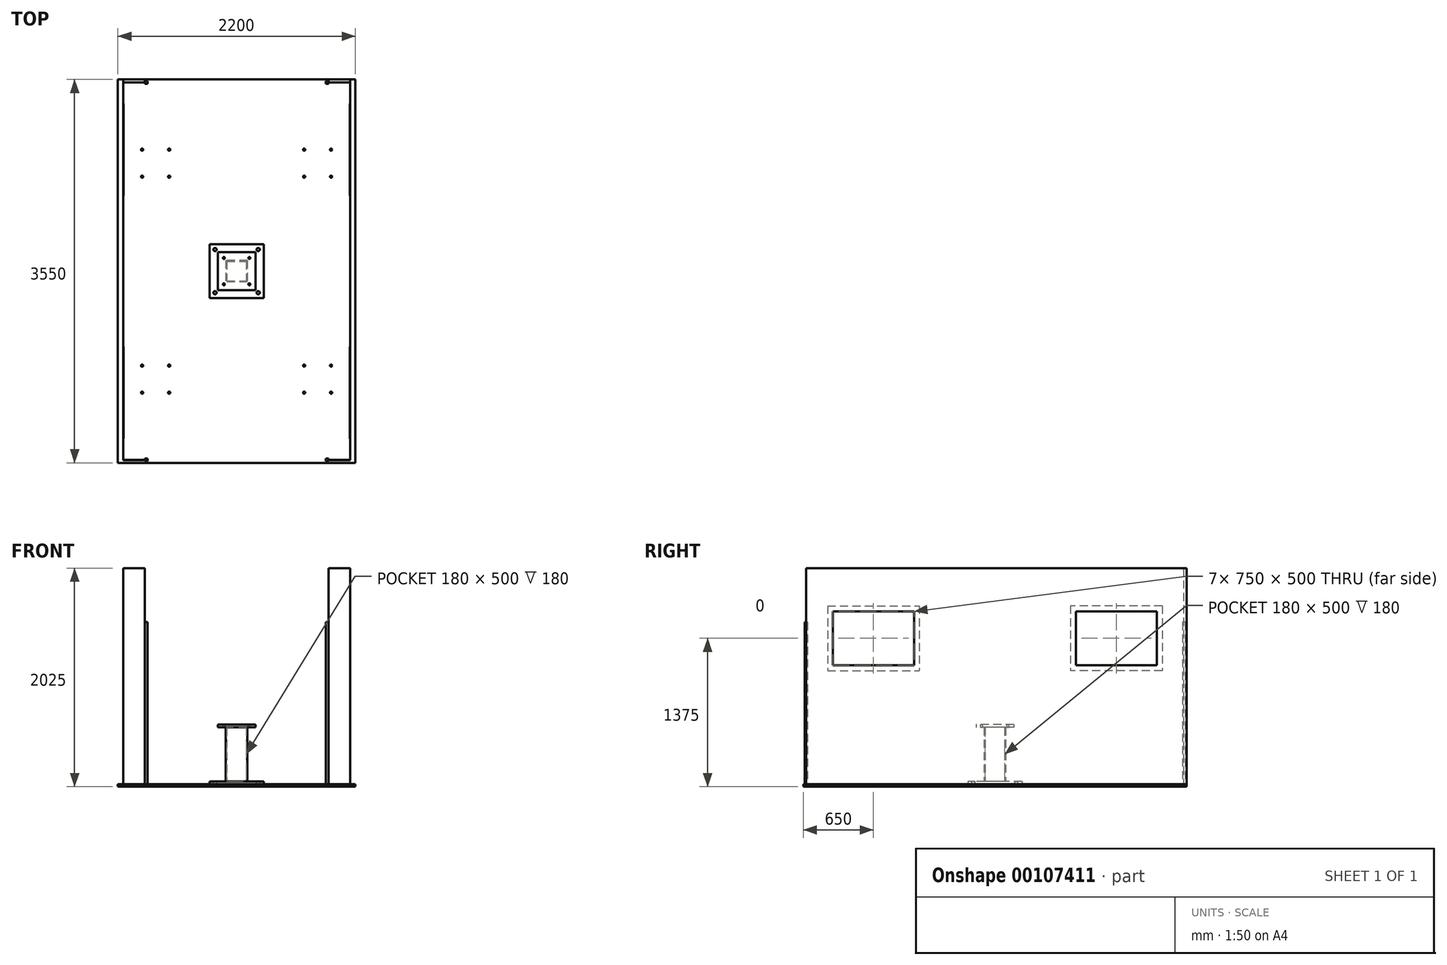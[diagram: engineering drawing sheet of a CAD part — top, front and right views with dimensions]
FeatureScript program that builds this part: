
annotation { "Feature Type Name" : "Feature", "Feature Type Description" : "" }
export const myFeature = defineFeature(function(context is Context, id is Id, definition is map)
    precondition{}
    {
        {
            var Q0;
            Q0=qCreatedBy(makeId("Top.planeOp"),FACE);
            var sketch = newSketch(context, id + "F0", { "sketchPlane" : qUnion([Q0])});
            skLineSegment(sketch, "E0.bottom", {"start": v(-1100, 1750) * mm, "end": v(1100, 1750) * mm});
            skLineSegment(sketch, "E0.top", {"start": v(-1100, -1750) * mm, "end": v(1100, -1750) * mm});
            skLineSegment(sketch, "E0.left", {"start": v(-1100, 1750) * mm, "end": v(-1100, -1750) * mm});
            skLineSegment(sketch, "E0.right", {"start": v(1100, 1750) * mm, "end": v(1100, -1750) * mm});
            skPoint(sketch, "E0.middle", {"position": v(0, 0) * mm});
            skSolve(sketch);
        }
        {
            var Q0;
            Q0 = qSketchRegion(id + "F0", true);
            extrude(context, id + "F1", {"entities" : qUnion([Q0]), "depth" : 25 * mm});
        }
        {
            var Q0;
            Q0=makeQuery(id+"F1.opExtrude","CAP_FACE",FACE,{"disambiguationData":[OSD([sQuery(id+"F0.wireOp",EDGE,"E0.bottom"),sQuery(id+"F0.wireOp",EDGE,"E0.top"),sQuery(id+"F0.wireOp",EDGE,"E0.left"),sQuery(id+"F0.wireOp",EDGE,"E0.right")])],"isStart":false});
            var sketch = newSketch(context, id + "F2", { "sketchPlane" : qUnion([Q0])});
            skLineSegment(sketch, "E1.bottom", {"start": v(-250, 250) * mm, "end": v(250, 250) * mm});
            skLineSegment(sketch, "E1.top", {"start": v(-250, -250) * mm, "end": v(250, -250) * mm});
            skLineSegment(sketch, "E1.left", {"start": v(-250, 250) * mm, "end": v(-250, -250) * mm});
            skLineSegment(sketch, "E1.right", {"start": v(250, 250) * mm, "end": v(250, -250) * mm});
            skPoint(sketch, "E1.middle", {"position": v(0, 0) * mm});
            skSolve(sketch);
        }
        {
            var Q0;
            Q0 = qSketchRegion(id + "F2", true);
            var Q1;
            Q1=makeQuery(id+"F2.imprint","IMPRINT",FACE,{"disambiguationData":[TD([[makeQuery(id+"F2.imprint","IMPRINT",EDGE,{"derivedFrom":sQuery(id+"F2.wireOp",EDGE,"E1.bottom")}),-1.0]])]});
            extrude(context, id + "F3", {"entities" : qUnion([Q0, Q1]), "depth" : 25 * mm});
        }
        {
            var Q0;
            Q0=makeQuery(id+"F3.opExtrude","CAP_FACE",FACE,{"disambiguationData":[OSD([sQuery(id+"F2.wireOp",EDGE,"E1.bottom"),sQuery(id+"F2.wireOp",EDGE,"E1.top"),sQuery(id+"F2.wireOp",EDGE,"E1.left"),sQuery(id+"F2.wireOp",EDGE,"E1.right")])],"isStart":false});
            var sketch = newSketch(context, id + "F4", { "sketchPlane" : qUnion([Q0])});
            skLineSegment(sketch, "E2.bottom", {"start": v(-200, 200) * mm, "end": v(200, 200) * mm, "construction": true});
            skLineSegment(sketch, "E2.top", {"start": v(-200, -200) * mm, "end": v(200, -200) * mm, "construction": true});
            skLineSegment(sketch, "E2.left", {"start": v(-200, 200) * mm, "end": v(-200, -200) * mm, "construction": true});
            skLineSegment(sketch, "E2.right", {"start": v(200, 200) * mm, "end": v(200, -200) * mm, "construction": true});
            skPoint(sketch, "E2.middle", {"position": v(0, 0) * mm});
            skCircle(sketch, "E3", {"center": v(-200, 200) * mm, "radius": 15 * mm});
            skCircle(sketch, "E4", {"center": v(200, 200) * mm, "radius": 15 * mm});
            skCircle(sketch, "E5", {"center": v(200, -200) * mm, "radius": 15 * mm});
            skCircle(sketch, "E6", {"center": v(-200, -200) * mm, "radius": 15 * mm});
            skSolve(sketch);
        }
        {
            var Q0;
            Q0 = qSketchRegion(id + "F4", true);
            extrude(context, id + "F5", {"entities" : qUnion([Q0]), "operationType" : NewBodyOperationType.REMOVE, "endBound" : BoundingType.THROUGH_ALL, "oppositeDirection" : true, "depth" : 25 * mm});
        }
        {
            var Q0;
            Q0=makeQuery(id+"F3.opExtrude","CAP_FACE",FACE,{"disambiguationData":[OSD([sQuery(id+"F2.wireOp",EDGE,"E1.bottom"),sQuery(id+"F2.wireOp",EDGE,"E1.top"),sQuery(id+"F2.wireOp",EDGE,"E1.left"),sQuery(id+"F2.wireOp",EDGE,"E1.right")])],"isStart":false});
            var sketch = newSketch(context, id + "F6", { "sketchPlane" : qUnion([Q0])});
            skLineSegment(sketch, "E7.bottom", {"start": v(100, 100) * mm, "end": v(-100, 100) * mm});
            skLineSegment(sketch, "E7.top", {"start": v(100, -100) * mm, "end": v(-100, -100) * mm});
            skLineSegment(sketch, "E7.left", {"start": v(100, 100) * mm, "end": v(100, -100) * mm});
            skLineSegment(sketch, "E7.right", {"start": v(-100, 100) * mm, "end": v(-100, -100) * mm});
            skPoint(sketch, "E7.middle", {"position": v(0, 0) * mm});
            skLineSegment(sketch, "E8.bottom", {"start": v(-90, 90) * mm, "end": v(90, 90) * mm});
            skLineSegment(sketch, "E8.top", {"start": v(-90, -90) * mm, "end": v(90, -90) * mm});
            skLineSegment(sketch, "E8.left", {"start": v(-90, 90) * mm, "end": v(-90, -90) * mm});
            skLineSegment(sketch, "E8.right", {"start": v(90, 90) * mm, "end": v(90, -90) * mm});
            skSolve(sketch);
        }
        {
            var Q0;
            Q0=makeQuery(id+"F6.imprint","IMPRINT",FACE,{"disambiguationData":[TD([[makeQuery(id+"F6.imprint","IMPRINT",EDGE,{"derivedFrom":sQuery(id+"F6.wireOp",EDGE,"E7.bottom")}),1.0]])]});
            extrude(context, id + "F7", {"entities" : qUnion([Q0]), "operationType" : NewBodyOperationType.ADD, "depth" : 500 * mm});
        }
        {
            var Q0;
            Q0=makeQuery(id+"F7.opExtrude","CAP_FACE",FACE,{"disambiguationData":[OSD([sQuery(id+"F6.wireOp",EDGE,"E7.bottom"),sQuery(id+"F6.wireOp",EDGE,"E7.top"),sQuery(id+"F6.wireOp",EDGE,"E7.left"),sQuery(id+"F6.wireOp",EDGE,"E7.right"),sQuery(id+"F6.wireOp",EDGE,"E8.bottom"),sQuery(id+"F6.wireOp",EDGE,"E8.top"),sQuery(id+"F6.wireOp",EDGE,"E8.left"),sQuery(id+"F6.wireOp",EDGE,"E8.right")])],"isStart":false});
            var sketch = newSketch(context, id + "F8", { "sketchPlane" : qUnion([Q0])});
            skLineSegment(sketch, "E9.bottom", {"start": v(175, 175) * mm, "end": v(-175, 175) * mm});
            skLineSegment(sketch, "E9.top", {"start": v(175, -175) * mm, "end": v(-175, -175) * mm});
            skLineSegment(sketch, "E9.left", {"start": v(175, 175) * mm, "end": v(175, -175) * mm});
            skLineSegment(sketch, "E9.right", {"start": v(-175, 175) * mm, "end": v(-175, -175) * mm});
            skPoint(sketch, "E9.middle", {"position": v(0, 0) * mm});
            skSolve(sketch);
        }
        {
            var Q0;
            Q0 = qSketchRegion(id + "F8", true);
            extrude(context, id + "F9", {"entities" : qUnion([Q0]), "operationType" : NewBodyOperationType.ADD, "depth" : 25 * mm});
        }
        {
            var Q0;
            Q0=makeQuery(id+"F1.opExtrude","CAP_FACE",FACE,{"disambiguationData":[OSD([sQuery(id+"F0.wireOp",EDGE,"E0.bottom"),sQuery(id+"F0.wireOp",EDGE,"E0.top"),sQuery(id+"F0.wireOp",EDGE,"E0.left"),sQuery(id+"F0.wireOp",EDGE,"E0.right")])],"isStart":false});
            var sketch = newSketch(context, id + "F10", { "sketchPlane" : qUnion([Q0])});
            skLineSegment(sketch, "E10.0", {"start": v(1100, 1750) * mm, "end": v(1100, -1750) * mm, "construction": true});
            skLineSegment(sketch, "E11.0", {"start": v(1050, 1750) * mm, "end": v(1050, -1748) * mm});
            skLineSegment(sketch, "E12", {"start": v(1050, 1750) * mm, "end": v(850, 1750) * mm});
            skLineSegment(sketch, "E13", {"start": v(1050, -1750) * mm, "end": v(850, -1750) * mm});
            skLineSegment(sketch, "E14", {"start": v(850, 1750) * mm, "end": v(850, 1748) * mm});
            skLineSegment(sketch, "E15", {"start": v(850, 1748) * mm, "end": v(1050, 1748) * mm});
            skLineSegment(sketch, "E16.0", {"start": v(1052, 1750) * mm, "end": v(1052, -1750) * mm});
            skLineSegment(sketch, "E17.0", {"start": v(1050, -1748) * mm, "end": v(850, -1748) * mm});
            skLineSegment(sketch, "E18", {"start": v(850, -1748) * mm, "end": v(850, -1750) * mm});
            skLineSegment(sketch, "E19", {"start": v(1052, -1750) * mm, "end": v(1050, -1750) * mm});
            skLineSegment(sketch, "E20", {"start": v(0, 1750) * mm, "end": v(0, -1750) * mm, "construction": true});
            skLineSegment(sketch, "E21.MirrorCS", {"start": v(-1052, -1750) * mm, "end": v(-1050, -1750) * mm});
            skLineSegment(sketch, "E22.MirrorCS", {"start": v(-850, 1750) * mm, "end": v(-850, 1748) * mm});
            skLineSegment(sketch, "E23.MirrorCS", {"start": v(-850, -1748) * mm, "end": v(-850, -1750) * mm});
            skLineSegment(sketch, "E24.MirrorCS", {"start": v(-1050, -1750) * mm, "end": v(-850, -1750) * mm});
            skLineSegment(sketch, "E25.MirrorCS", {"start": v(-1050, -1748) * mm, "end": v(-850, -1748) * mm});
            skLineSegment(sketch, "E26.MirrorCS", {"start": v(-1050, 1750) * mm, "end": v(-850, 1750) * mm});
            skLineSegment(sketch, "E27.MirrorCS", {"start": v(-1050, 1750) * mm, "end": v(-1050, -1748) * mm});
            skLineSegment(sketch, "E28.MirrorCS", {"start": v(-1100, 1750) * mm, "end": v(-1100, -1750) * mm, "construction": true});
            skLineSegment(sketch, "E29.MirrorCS", {"start": v(-850, 1748) * mm, "end": v(-1050, 1748) * mm});
            skLineSegment(sketch, "E30.MirrorCS", {"start": v(-1052, 1750) * mm, "end": v(-1052, -1750) * mm});
            skSolve(sketch);
        }
        {
            var Q0;
            Q0 = qSketchRegion(id + "F10", true);
            var Q1;
            Q1=makeQuery(id+"F10.imprint","IMPRINT",FACE,{"disambiguationData":[TD([[makeQuery(id+"F10.imprint","IMPRINT",EDGE,{"derivedFrom":sQuery(id+"F10.wireOp",EDGE,"E21.MirrorCS")}),1.0]])]});
            var Q2;
            Q2=makeQuery(id+"F10.imprint","IMPRINT",FACE,{"disambiguationData":[TD([[makeQuery(id+"F10.imprint","IMPRINT",EDGE,{"derivedFrom":sQuery(id+"F10.wireOp",EDGE,"E13")}),1.0]])]});
            extrude(context, id + "F11", {"entities" : qUnion([Q0, Q1, Q2]), "depth" : 2000 * mm});
        }
        {
            var Q0;
            Q0=makeQuery(id+"F11.opExtrude","SWEPT_FACE",FACE,{"disambiguationData":[OSD([sQuery(id+"F10.wireOp",EDGE,"E16.0")])]});
            var sketch = newSketch(context, id + "F12", { "sketchPlane" : qUnion([Q0])});
            skLineSegment(sketch, "E31.bottom", {"start": v(-1500, 1625) * mm, "end": v(-750, 1625) * mm});
            skLineSegment(sketch, "E31.top", {"start": v(-1500, 1125) * mm, "end": v(-750, 1125) * mm});
            skLineSegment(sketch, "E31.left", {"start": v(-1500, 1625) * mm, "end": v(-1500, 1125) * mm});
            skLineSegment(sketch, "E31.right", {"start": v(-750, 1625) * mm, "end": v(-750, 1125) * mm});
            skLineSegment(sketch, "E32", {"start": v(0, 0) * mm, "end": v(0, 2025) * mm, "construction": true});
            skLineSegment(sketch, "E33.MirrorCS", {"start": v(1500, 1625) * mm, "end": v(750, 1625) * mm});
            skLineSegment(sketch, "E34.MirrorCS", {"start": v(1500, 1125) * mm, "end": v(750, 1125) * mm});
            skLineSegment(sketch, "E35.MirrorCS", {"start": v(1500, 1625) * mm, "end": v(1500, 1125) * mm});
            skLineSegment(sketch, "E36.MirrorCS", {"start": v(750, 1625) * mm, "end": v(750, 1125) * mm});
            skSolve(sketch);
        }
        {
            var Q0;
            Q0=makeQuery(id+"F11.opExtrude","SWEPT_FACE",FACE,{"disambiguationData":[OSD([sQuery(id+"F10.wireOp",EDGE,"E30.MirrorCS")])]});
            var sketch = newSketch(context, id + "F13", { "sketchPlane" : qUnion([Q0])});
            skLineSegment(sketch, "E37.0", {"start": v(-1500, 1625) * mm, "end": v(-750, 1625) * mm});
            skLineSegment(sketch, "E37.1", {"start": v(-1500, 1125) * mm, "end": v(-750, 1125) * mm});
            skLineSegment(sketch, "E37.2", {"start": v(-1500, 1625) * mm, "end": v(-1500, 1125) * mm});
            skLineSegment(sketch, "E37.3", {"start": v(-750, 1625) * mm, "end": v(-750, 1125) * mm});
            skLineSegment(sketch, "E38.0", {"start": v(1500, 1625) * mm, "end": v(750, 1625) * mm});
            skLineSegment(sketch, "E38.1", {"start": v(1500, 1125) * mm, "end": v(750, 1125) * mm});
            skLineSegment(sketch, "E38.2", {"start": v(1500, 1625) * mm, "end": v(1500, 1125) * mm});
            skLineSegment(sketch, "E38.3", {"start": v(750, 1625) * mm, "end": v(750, 1125) * mm});
            skLineSegment(sketch, "E39.0", {"start": v(0, 0) * mm, "end": v(0, 2025) * mm, "construction": true});
            skSolve(sketch);
        }
        {
            var Q0;
            Q0=makeQuery(id+"F13.imprint","IMPRINT",FACE,{"disambiguationData":[TD([[makeQuery(id+"F13.imprint","IMPRINT",EDGE,{"derivedFrom":sQuery(id+"F13.wireOp",EDGE,"E38.0")}),1.0]])]});
            var Q1;
            Q1=makeQuery(id+"F13.imprint","IMPRINT",FACE,{"disambiguationData":[TD([[makeQuery(id+"F13.imprint","IMPRINT",EDGE,{"derivedFrom":sQuery(id+"F13.wireOp",EDGE,"E37.0")}),-1.0]])]});
            var Q2;
            Q2=makeQuery(id+"F11.opExtrude","SWEPT_FACE",FACE,{"disambiguationData":[OSD([sQuery(id+"F10.wireOp",EDGE,"E27.MirrorCS")])]});
            extrude(context, id + "F14", {"entities" : qUnion([Q0, Q1]), "operationType" : NewBodyOperationType.REMOVE, "endBound" : BoundingType.UP_TO_SURFACE, "oppositeDirection" : true, "endBoundEntityFace" : qUnion([Q2]), "depth" : 25 * mm});
        }
        {
            var Q0;
            Q0=makeQuery(id+"F12.imprint","IMPRINT",FACE,{"disambiguationData":[TD([[makeQuery(id+"F12.imprint","IMPRINT",EDGE,{"derivedFrom":sQuery(id+"F12.wireOp",EDGE,"E31.bottom")}),-1.0]])]});
            var Q1;
            Q1=makeQuery(id+"F12.imprint","IMPRINT",FACE,{"disambiguationData":[TD([[makeQuery(id+"F12.imprint","IMPRINT",EDGE,{"derivedFrom":sQuery(id+"F12.wireOp",EDGE,"E33.MirrorCS")}),1.0]])]});
            var Q2;
            Q2=makeQuery(id+"F11.opExtrude","SWEPT_FACE",FACE,{"disambiguationData":[OSD([sQuery(id+"F10.wireOp",EDGE,"E11.0")])]});
            extrude(context, id + "F15", {"entities" : qUnion([Q0, Q1]), "operationType" : NewBodyOperationType.REMOVE, "endBound" : BoundingType.UP_TO_SURFACE, "oppositeDirection" : true, "endBoundEntityFace" : qUnion([Q2]), "depth" : 25 * mm});
        }
        {
            var Q0;
            Q0=makeQuery(id+"F11.opExtrude","SWEPT_FACE",FACE,{"disambiguationData":[OSD([sQuery(id+"F10.wireOp",EDGE,"E27.MirrorCS")])]});
            var sketch = newSketch(context, id + "F16", { "sketchPlane" : qUnion([Q0])});
            skLineSegment(sketch, "E40.bottom", {"start": v(-1550, 1675) * mm, "end": v(-700, 1675) * mm});
            skLineSegment(sketch, "E40.top", {"start": v(-1550, 1075) * mm, "end": v(-700, 1075) * mm});
            skLineSegment(sketch, "E40.left", {"start": v(-1550, 1675) * mm, "end": v(-1550, 1075) * mm});
            skLineSegment(sketch, "E40.right", {"start": v(-700, 1675) * mm, "end": v(-700, 1075) * mm});
            skLineSegment(sketch, "E41.0", {"start": v(-1500, 1625) * mm, "end": v(-750, 1625) * mm, "construction": true});
            skLineSegment(sketch, "E42.0", {"start": v(-1500, 1125) * mm, "end": v(-750, 1125) * mm, "construction": true});
            skLineSegment(sketch, "E43.0", {"start": v(-1500, 1625) * mm, "end": v(-1500, 1125) * mm, "construction": true});
            skLineSegment(sketch, "E44.0", {"start": v(-750, 1625) * mm, "end": v(-750, 1125) * mm, "construction": true});
            skLineSegment(sketch, "E45", {"start": v(0, 2025) * mm, "end": v(0, 0) * mm, "construction": true});
            skLineSegment(sketch, "E46.MirrorCS", {"start": v(700, 1675) * mm, "end": v(700, 1075) * mm});
            skLineSegment(sketch, "E47.MirrorCS", {"start": v(1550, 1675) * mm, "end": v(700, 1675) * mm});
            skLineSegment(sketch, "E48.MirrorCS", {"start": v(750, 1625) * mm, "end": v(750, 1125) * mm});
            skLineSegment(sketch, "E49.MirrorCS", {"start": v(1500, 1625) * mm, "end": v(1500, 1125) * mm});
            skLineSegment(sketch, "E50.MirrorCS", {"start": v(1500, 1625) * mm, "end": v(750, 1625) * mm});
            skLineSegment(sketch, "E51.MirrorCS", {"start": v(1500, 1125) * mm, "end": v(750, 1125) * mm});
            skLineSegment(sketch, "E52.MirrorCS", {"start": v(1550, 1075) * mm, "end": v(700, 1075) * mm});
            skLineSegment(sketch, "E53.MirrorCS", {"start": v(1550, 1675) * mm, "end": v(1550, 1075) * mm});
            skSolve(sketch);
        }
        {
            var Q0;
            Q0=makeQuery(id+"F16.imprint","IMPRINT",FACE,{"disambiguationData":[TD([[makeQuery(id+"F16.imprint","IMPRINT",EDGE,{"derivedFrom":makeQuery(id+"F14.boolean.opBoolean","COPY",EDGE,{"derivedFrom":makeQuery(id+"F14.opExtrude","CAP_EDGE",EDGE,{"disambiguationData":[OSD([sQuery(id+"F13.wireOp",EDGE,"E38.0")])],"isStart":false})})}),-1.0]])]});
            var Q1;
            Q1=makeQuery(id+"F16.imprint","IMPRINT",FACE,{"disambiguationData":[TD([[makeQuery(id+"F16.imprint","IMPRINT",EDGE,{"derivedFrom":sQuery(id+"F16.wireOp",EDGE,"E40.bottom")}),-1.0]])]});
            var Q2;
            Q2=makeQuery(id+"F16.imprint","IMPRINT",FACE,{"disambiguationData":[TD([[makeQuery(id+"F16.imprint","IMPRINT",EDGE,{"derivedFrom":sQuery(id+"F16.wireOp",EDGE,"E48.MirrorCS")}),-1.0]])]});
            var Q3;
            Q3=makeQuery(id+"F16.imprint","IMPRINT",FACE,{"disambiguationData":[TD([[makeQuery(id+"F16.imprint","IMPRINT",EDGE,{"derivedFrom":sQuery(id+"F16.wireOp",EDGE,"E48.MirrorCS")}),1.0]])]});
            extrude(context, id + "F17", {"entities" : qUnion([Q0, Q1, Q2, Q3]), "depth" : 2 * mm});
        }
        {
            var Q0;
            Q0=makeQuery(id+"F11.opExtrude","SWEPT_FACE",FACE,{"disambiguationData":[OSD([sQuery(id+"F10.wireOp",EDGE,"E11.0")])]});
            var sketch = newSketch(context, id + "F18", { "sketchPlane" : qUnion([Q0])});
            skLineSegment(sketch, "E54.bottom", {"start": v(-1550, 1675) * mm, "end": v(-700, 1675) * mm});
            skLineSegment(sketch, "E54.top", {"start": v(-1550, 1075) * mm, "end": v(-700, 1075) * mm});
            skLineSegment(sketch, "E54.left", {"start": v(-1550, 1675) * mm, "end": v(-1550, 1075) * mm});
            skLineSegment(sketch, "E54.right", {"start": v(-700, 1675) * mm, "end": v(-700, 1075) * mm});
            skLineSegment(sketch, "E55", {"start": v(0, 2025) * mm, "end": v(0, 0) * mm, "construction": true});
            skLineSegment(sketch, "E56.MirrorCS", {"start": v(1550, 1675) * mm, "end": v(700, 1675) * mm});
            skLineSegment(sketch, "E57.MirrorCS", {"start": v(1550, 1075) * mm, "end": v(700, 1075) * mm});
            skLineSegment(sketch, "E58.MirrorCS", {"start": v(1550, 1675) * mm, "end": v(1550, 1075) * mm});
            skLineSegment(sketch, "E59.MirrorCS", {"start": v(700, 1675) * mm, "end": v(700, 1075) * mm});
            skSolve(sketch);
        }
        {
            var Q0;
            Q0=makeQuery(id+"F18.imprint","IMPRINT",FACE,{"disambiguationData":[TD([[makeQuery(id+"F18.imprint","IMPRINT",EDGE,{"derivedFrom":makeQuery(id+"F15.boolean.opBoolean","COPY",EDGE,{"derivedFrom":makeQuery(id+"F15.opExtrude","CAP_EDGE",EDGE,{"disambiguationData":[OSD([sQuery(id+"F12.wireOp",EDGE,"E31.bottom")])],"isStart":false})})}),-1.0]])]});
            var Q1;
            Q1=makeQuery(id+"F18.imprint","IMPRINT",FACE,{"disambiguationData":[TD([[makeQuery(id+"F18.imprint","IMPRINT",EDGE,{"derivedFrom":sQuery(id+"F18.wireOp",EDGE,"E54.bottom")}),-1.0]])]});
            var Q2;
            Q2=makeQuery(id+"F18.imprint","IMPRINT",FACE,{"disambiguationData":[TD([[makeQuery(id+"F18.imprint","IMPRINT",EDGE,{"derivedFrom":sQuery(id+"F18.wireOp",EDGE,"E56.MirrorCS")}),1.0]])]});
            var Q3;
            Q3=makeQuery(id+"F18.imprint","IMPRINT",FACE,{"disambiguationData":[TD([[makeQuery(id+"F18.imprint","IMPRINT",EDGE,{"derivedFrom":makeQuery(id+"F15.boolean.opBoolean","COPY",EDGE,{"derivedFrom":makeQuery(id+"F15.opExtrude","CAP_EDGE",EDGE,{"disambiguationData":[OSD([sQuery(id+"F12.wireOp",EDGE,"E33.MirrorCS")])],"isStart":false})})}),1.0]])]});
            extrude(context, id + "F19", {"entities" : qUnion([Q0, Q1, Q2, Q3]), "depth" : 2 * mm});
        }
        {
            var Q0;
            Q0=makeQuery(id+"F1.opExtrude","CAP_FACE",FACE,{"disambiguationData":[OSD([sQuery(id+"F0.wireOp",EDGE,"E0.bottom"),sQuery(id+"F0.wireOp",EDGE,"E0.top"),sQuery(id+"F0.wireOp",EDGE,"E0.left"),sQuery(id+"F0.wireOp",EDGE,"E0.right")])],"isStart":false});
            var sketch = newSketch(context, id + "F20", { "sketchPlane" : qUnion([Q0])});
            skLineSegment(sketch, "E60", {"start": v(0, 1750) * mm, "end": v(0, -1750) * mm, "construction": true});
            skLineSegment(sketch, "E61", {"start": v(0, 1000) * mm, "end": v(-989.51, 1000) * mm, "construction": true});
            skLineSegment(sketch, "E62.MirrorCS", {"start": v(0, 1000) * mm, "end": v(989.51, 1000) * mm, "construction": true});
            skLineSegment(sketch, "E63", {"start": v(0, 0) * mm, "end": v(-1100, 0) * mm, "construction": true});
            skLineSegment(sketch, "E64.MirrorCS", {"start": v(0, 0) * mm, "end": v(1100, 0) * mm, "construction": true});
            skLineSegment(sketch, "E65.MirrorCS", {"start": v(0, -1000) * mm, "end": v(-989.51, -1000) * mm, "construction": true});
            skLineSegment(sketch, "E66.MirrorCS", {"start": v(0, -1000) * mm, "end": v(989.51, -1000) * mm, "construction": true});
            skLineSegment(sketch, "E67", {"start": v(-875, 875) * mm, "end": v(-875, 1125) * mm, "construction": true});
            skLineSegment(sketch, "E68.0", {"start": v(-625, 875) * mm, "end": v(-625, 1125) * mm, "construction": true});
            skCircle(sketch, "E69", {"center": v(-625, 1125) * mm, "radius": 10 * mm});
            skCircle(sketch, "E70", {"center": v(-875, 1125) * mm, "radius": 10 * mm});
            skCircle(sketch, "E71", {"center": v(-625, 875) * mm, "radius": 10 * mm});
            skCircle(sketch, "E72", {"center": v(-875, 875) * mm, "radius": 10 * mm});
            skCircle(sketch, "E73.MirrorC", {"center": v(875, 875) * mm, "radius": 10 * mm});
            skCircle(sketch, "E74.MirrorC", {"center": v(625, 875) * mm, "radius": 10 * mm});
            skCircle(sketch, "E75.MirrorC", {"center": v(625, 1125) * mm, "radius": 10 * mm});
            skCircle(sketch, "E76.MirrorC", {"center": v(875, 1125) * mm, "radius": 10 * mm});
            skLineSegment(sketch, "E77.MirrorCS", {"start": v(875, 875) * mm, "end": v(875, 1125) * mm, "construction": true});
            skLineSegment(sketch, "E78.MirrorCS", {"start": v(625, 875) * mm, "end": v(625, 1125) * mm, "construction": true});
            skCircle(sketch, "E79.MirrorC", {"center": v(875, -1125) * mm, "radius": 10 * mm});
            skCircle(sketch, "E80.MirrorC", {"center": v(-875, -875) * mm, "radius": 10 * mm});
            skCircle(sketch, "E81.MirrorC", {"center": v(-625, -875) * mm, "radius": 10 * mm});
            skCircle(sketch, "E82.MirrorC", {"center": v(-625, -1125) * mm, "radius": 10 * mm});
            skCircle(sketch, "E83.MirrorC", {"center": v(-875, -1125) * mm, "radius": 10 * mm});
            skCircle(sketch, "E84.MirrorC", {"center": v(875, -875) * mm, "radius": 10 * mm});
            skCircle(sketch, "E85.MirrorC", {"center": v(625, -875) * mm, "radius": 10 * mm});
            skCircle(sketch, "E86.MirrorC", {"center": v(625, -1125) * mm, "radius": 10 * mm});
            skLineSegment(sketch, "E87.MirrorCS", {"start": v(-625, -875) * mm, "end": v(-625, -1125) * mm, "construction": true});
            skLineSegment(sketch, "E88.MirrorCS", {"start": v(625, -875) * mm, "end": v(625, -1125) * mm, "construction": true});
            skLineSegment(sketch, "E89.MirrorCS", {"start": v(-875, -875) * mm, "end": v(-875, -1125) * mm, "construction": true});
            skLineSegment(sketch, "E90.MirrorCS", {"start": v(875, -875) * mm, "end": v(875, -1125) * mm, "construction": true});
            skSolve(sketch);
        }
        {
            var Q0;
            Q0 = qSketchRegion(id + "F20", true);
            var Q1;
            Q1=makeQuery(id+"F1.opExtrude","CAP_FACE",FACE,{"disambiguationData":[OSD([sQuery(id+"F0.wireOp",EDGE,"E0.bottom"),sQuery(id+"F0.wireOp",EDGE,"E0.top"),sQuery(id+"F0.wireOp",EDGE,"E0.left"),sQuery(id+"F0.wireOp",EDGE,"E0.right")])],"isStart":true});
            var Q2;
            Q2=makeQuery(id+"F1.opExtrude","SWEPT_BODY",BODY,{"disambiguationData":[OSD([sQuery(id+"F0.wireOp",EDGE,"E0.bottom"),sQuery(id+"F0.wireOp",EDGE,"E0.top"),sQuery(id+"F0.wireOp",EDGE,"E0.left"),sQuery(id+"F0.wireOp",EDGE,"E0.right")])]});
            extrude(context, id + "F21", {"entities" : qUnion([Q0]), "operationType" : NewBodyOperationType.REMOVE, "endBound" : BoundingType.UP_TO_BODY, "oppositeDirection" : true, "endBoundEntityFace" : qUnion([Q1]), "endBoundEntityBody" : qUnion([Q2]), "depth" : 25 * mm});
        }
        {
            var Q0;
            Q0=makeQuery(id+"F9.opExtrude","CAP_FACE",FACE,{"disambiguationData":[OSD([sQuery(id+"F8.wireOp",EDGE,"E9.bottom"),sQuery(id+"F8.wireOp",EDGE,"E9.top"),sQuery(id+"F8.wireOp",EDGE,"E9.left"),sQuery(id+"F8.wireOp",EDGE,"E9.right")])],"isStart":false});
            var sketch = newSketch(context, id + "F22", { "sketchPlane" : qUnion([Q0])});
            skLineSegment(sketch, "E91.bottom", {"start": v(-118, 122) * mm, "end": v(118, 122) * mm, "construction": true});
            skLineSegment(sketch, "E91.top", {"start": v(-118, -122) * mm, "end": v(118, -122) * mm, "construction": true});
            skLineSegment(sketch, "E91.left", {"start": v(-118, 122) * mm, "end": v(-118, -122) * mm, "construction": true});
            skLineSegment(sketch, "E91.right", {"start": v(118, 122) * mm, "end": v(118, -122) * mm, "construction": true});
            skPoint(sketch, "E91.middle", {"position": v(0, 0) * mm});
            skCircle(sketch, "E92", {"center": v(-118, 122) * mm, "radius": 9 * mm});
            skCircle(sketch, "E93", {"center": v(118, 122) * mm, "radius": 9 * mm});
            skCircle(sketch, "E94", {"center": v(-118, -122) * mm, "radius": 9 * mm});
            skCircle(sketch, "E95", {"center": v(118, -122) * mm, "radius": 9 * mm});
            skSolve(sketch);
        }
        {
            var Q0;
            Q0 = qSketchRegion(id + "F22", true);
            var Q1;
            {var subQ0=sQuery(id+"F8.wireOp",EDGE,"E9.bottom");var subQ1=sQuery(id+"F8.wireOp",EDGE,"E9.top");var subQ2=sQuery(id+"F8.wireOp",EDGE,"E9.left");var subQ3=sQuery(id+"F8.wireOp",EDGE,"E9.right");Q1=makeQuery(id+"F9.boolean.opBoolean","SPLIT",FACE,{"disambiguationData":[TD([makeQuery(id+"F7.opExtrude","SWEPT_FACE",FACE,{"disambiguationData":[OSD([sQuery(id+"F6.wireOp",EDGE,"E7.bottom")])]})])],"derivedFrom":makeQuery(id+"F9.opExtrude","CAP_FACE",FACE,{"disambiguationData":[OSD([subQ0,subQ1,subQ2,subQ3])],"isStart":true})});}
            extrude(context, id + "F23", {"entities" : qUnion([Q0]), "operationType" : NewBodyOperationType.REMOVE, "endBound" : BoundingType.UP_TO_SURFACE, "oppositeDirection" : true, "endBoundEntityFace" : qUnion([Q1]), "depth" : 25 * mm});
        }
        {
            var Q0;
            Q0=makeQuery(id+"F1.opExtrude","SWEPT_FACE",FACE,{"disambiguationData":[OSD([sQuery(id+"F0.wireOp",EDGE,"E0.top")])]});
            extrude(context, id + "F24", {"entities" : qUnion([Q0]), "operationType" : NewBodyOperationType.ADD, "depth" : 25 * mm});
        }
        {
            var Q0;
            Q0=makeQuery(id+"F1.opExtrude","SWEPT_FACE",FACE,{"disambiguationData":[OSD([sQuery(id+"F0.wireOp",EDGE,"E0.bottom")])]});
            extrude(context, id + "F25", {"entities" : qUnion([Q0]), "operationType" : NewBodyOperationType.ADD, "depth" : 25 * mm});
        }
        {
            var Q0;
            {var subQ0=sQuery(id+"F0.wireOp",EDGE,"E0.bottom");var subQ1=sQuery(id+"F0.wireOp",EDGE,"E0.top");Q0=makeQuery(id+"F25.boolean.opBoolean","MERGE",FACE,{"derivedFrom":[makeQuery(id+"F24.boolean.opBoolean","MERGE",FACE,{"derivedFrom":[makeQuery(id+"F1.opExtrude","CAP_FACE",FACE,{"disambiguationData":[OSD([subQ0,subQ1,sQuery(id+"F0.wireOp",EDGE,"E0.left"),sQuery(id+"F0.wireOp",EDGE,"E0.right")])],"isStart":false}),makeQuery(id+"F24.opExtrude","SWEPT_FACE",FACE,{"disambiguationData":[OSD([subQ1]),TDD([makeQuery(id+"F1.opExtrude","CAP_EDGE",EDGE,{"disambiguationData":[OSD([subQ1])],"isStart":false})])]})]}),makeQuery(id+"F25.opExtrude","SWEPT_FACE",FACE,{"disambiguationData":[OSD([subQ0]),TDD([makeQuery(id+"F1.opExtrude","CAP_EDGE",EDGE,{"disambiguationData":[OSD([subQ0])],"isStart":false})])]})]});}
            var sketch = newSketch(context, id + "F26", { "sketchPlane" : qUnion([Q0])});
            skLineSegment(sketch, "E96.0", {"start": v(850, 1750) * mm, "end": v(850, 1748) * mm});
            skLineSegment(sketch, "E97.0", {"start": v(-850, 1750) * mm, "end": v(-850, 1748) * mm});
            skLineSegment(sketch, "E98", {"start": v(-850, 1749) * mm, "end": v(-850, 1736.5) * mm});
            skLineSegment(sketch, "E99", {"start": v(-850, 1736.5) * mm, "end": v(-825, 1736.5) * mm});
            skLineSegment(sketch, "E100", {"start": v(-825, 1736.5) * mm, "end": v(-825, 1749) * mm});
            skLineSegment(sketch, "E101", {"start": v(-825, 1749) * mm, "end": v(-850, 1749) * mm, "construction": true});
            skLineSegment(sketch, "E102.MirrorCS", {"start": v(-850, 1748) * mm, "end": v(-850, 1750) * mm});
            skLineSegment(sketch, "E103.MirrorCS", {"start": v(-825, 1761.5) * mm, "end": v(-825, 1749) * mm});
            skLineSegment(sketch, "E104.MirrorCS", {"start": v(-850, 1761.5) * mm, "end": v(-825, 1761.5) * mm});
            skLineSegment(sketch, "E105.MirrorCS", {"start": v(-850, 1749) * mm, "end": v(-850, 1761.5) * mm});
            skLineSegment(sketch, "E106", {"start": v(0, 1775) * mm, "end": v(0, 1024.06) * mm, "construction": true});
            skLineSegment(sketch, "E107.0", {"start": v(-1100, 1775) * mm, "end": v(1100, 1775) * mm});
            skLineSegment(sketch, "E108", {"start": v(850, 1749) * mm, "end": v(850, 1736.5) * mm});
            skLineSegment(sketch, "E109", {"start": v(850, 1736.5) * mm, "end": v(825, 1736.5) * mm});
            skLineSegment(sketch, "E110", {"start": v(825, 1736.5) * mm, "end": v(825, 1761.5) * mm});
            skLineSegment(sketch, "E111", {"start": v(825, 1761.5) * mm, "end": v(850, 1761.5) * mm});
            skLineSegment(sketch, "E112", {"start": v(850, 1761.5) * mm, "end": v(850, 1749) * mm});
            skLineSegment(sketch, "E113", {"start": v(1100, 0) * mm, "end": v(-1100, 0) * mm, "construction": true});
            skLineSegment(sketch, "E114.MirrorCS", {"start": v(-850, -1750) * mm, "end": v(-850, -1748) * mm});
            skLineSegment(sketch, "E115.MirrorCS", {"start": v(-850, -1748) * mm, "end": v(-850, -1750) * mm});
            skLineSegment(sketch, "E116.MirrorCS", {"start": v(-850, -1749) * mm, "end": v(-850, -1736.5) * mm});
            skLineSegment(sketch, "E117.MirrorCS", {"start": v(-850, -1749) * mm, "end": v(-850, -1761.5) * mm});
            skLineSegment(sketch, "E118.MirrorCS", {"start": v(-825, -1749) * mm, "end": v(-850, -1749) * mm, "construction": true});
            skLineSegment(sketch, "E119.MirrorCS", {"start": v(-825, -1761.5) * mm, "end": v(-825, -1749) * mm});
            skLineSegment(sketch, "E120.MirrorCS", {"start": v(-825, -1736.5) * mm, "end": v(-825, -1749) * mm});
            skLineSegment(sketch, "E121.MirrorCS", {"start": v(-850, -1761.5) * mm, "end": v(-825, -1761.5) * mm});
            skLineSegment(sketch, "E122.MirrorCS", {"start": v(-850, -1736.5) * mm, "end": v(-825, -1736.5) * mm});
            skLineSegment(sketch, "E123.MirrorCS", {"start": v(850, -1749) * mm, "end": v(850, -1736.5) * mm});
            skLineSegment(sketch, "E124.MirrorCS", {"start": v(850, -1736.5) * mm, "end": v(825, -1736.5) * mm});
            skLineSegment(sketch, "E125.MirrorCS", {"start": v(825, -1736.5) * mm, "end": v(825, -1761.5) * mm});
            skLineSegment(sketch, "E126.MirrorCS", {"start": v(825, -1761.5) * mm, "end": v(850, -1761.5) * mm});
            skLineSegment(sketch, "E127.MirrorCS", {"start": v(850, -1750) * mm, "end": v(850, -1748) * mm});
            skLineSegment(sketch, "E128.MirrorCS", {"start": v(850, -1761.5) * mm, "end": v(850, -1749) * mm});
            skLineSegment(sketch, "E129.MirrorCS", {"start": v(-1100, -1775) * mm, "end": v(1100, -1775) * mm});
            skSolve(sketch);
        }
        {
            var Q0;
            {var subQ0=sQuery(id+"F26.wireOp",EDGE,"E109");Q0=makeQuery(id+"F26.imprint","IMPRINT",FACE,{"disambiguationData":[TD([[makeQuery(id+"F26.imprint","IMPRINT",EDGE,{"derivedFrom":subQ0}),-1.0]])]});}
            var Q1;
            Q1=makeQuery(id+"F26.imprint","IMPRINT",FACE,{"disambiguationData":[TD([[makeQuery(id+"F26.imprint","IMPRINT",EDGE,{"derivedFrom":sQuery(id+"F26.wireOp",EDGE,"E98")}),1.0]])]});
            var Q2;
            Q2=makeQuery(id+"F26.imprint","IMPRINT",FACE,{"disambiguationData":[TD([[makeQuery(id+"F26.imprint","IMPRINT",EDGE,{"derivedFrom":sQuery(id+"F26.wireOp",EDGE,"E119.MirrorCS")}),1.0]])]});
            var Q3;
            Q3=makeQuery(id+"F26.imprint","IMPRINT",FACE,{"disambiguationData":[TD([[makeQuery(id+"F26.imprint","IMPRINT",EDGE,{"derivedFrom":sQuery(id+"F26.wireOp",EDGE,"E123.MirrorCS")}),1.0]])]});
            extrude(context, id + "F27", {"entities" : qUnion([Q0, Q1, Q2, Q3]), "depth" : 1500 * mm});
        }
    });
